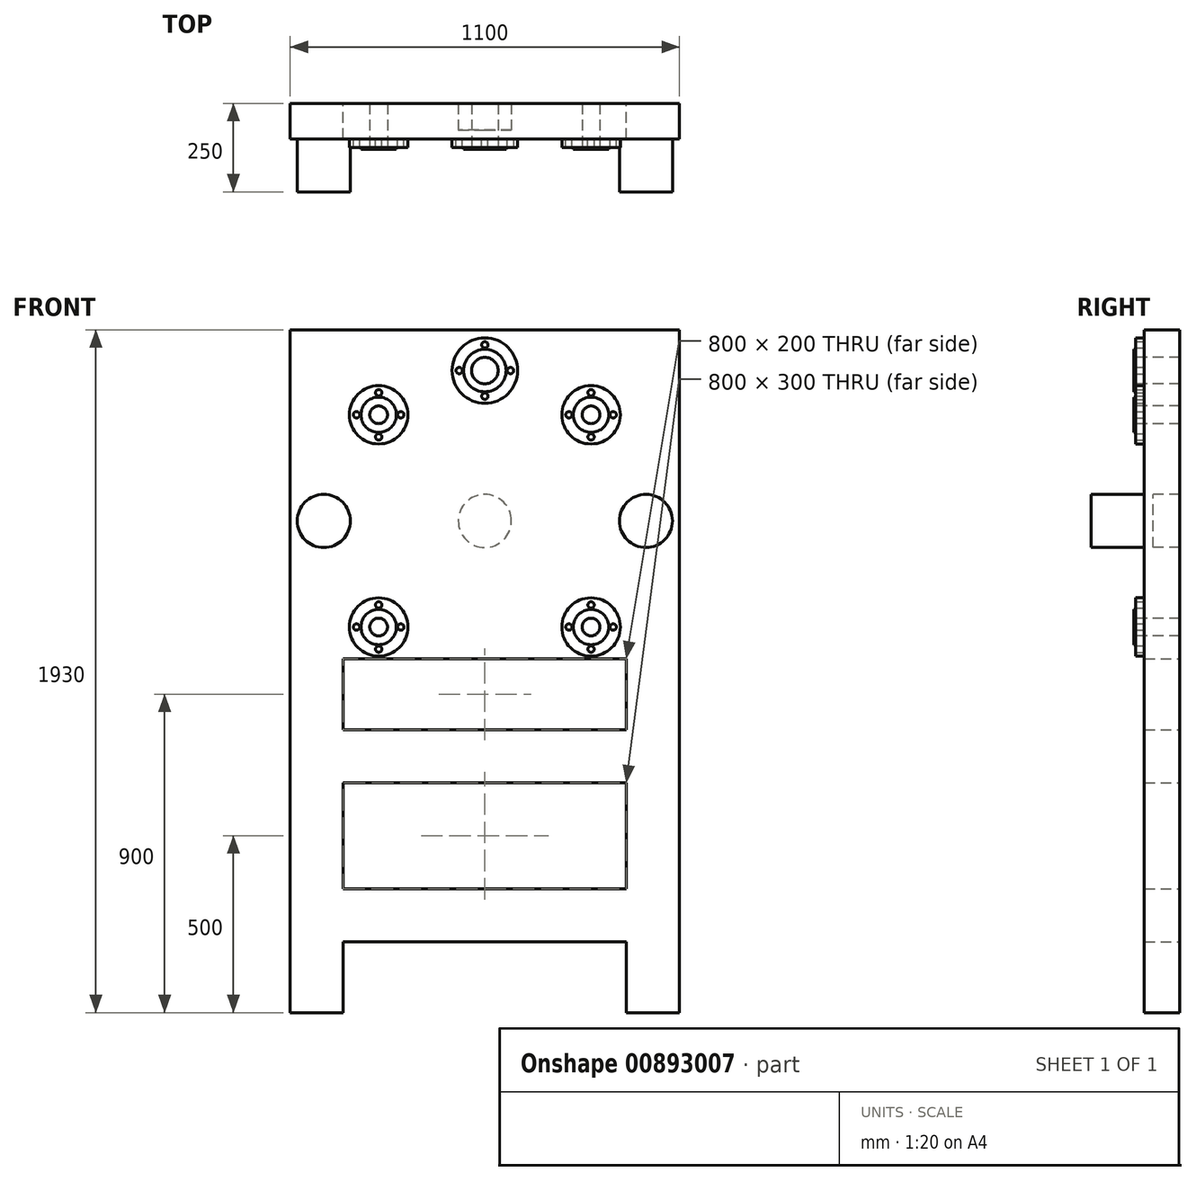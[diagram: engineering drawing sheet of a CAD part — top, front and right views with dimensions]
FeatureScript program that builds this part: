
annotation { "Feature Type Name" : "Feature", "Feature Type Description" : "" }
export const myFeature = defineFeature(function(context is Context, id is Id, definition is map)
    precondition{}
    {
        {
            var Q0;
            Q0=qCreatedBy(makeId("Front.planeOp"),FACE);
            var sketch = newSketch(context, id + "F0", { "sketchPlane" : qUnion([Q0])});
            skLineSegment(sketch, "E0.bottom", {"start": v(550, -965) * mm, "end": v(400, -965) * mm});
            skLineSegment(sketch, "E0.top", {"start": v(550, 965) * mm, "end": v(-550, 965) * mm});
            skLineSegment(sketch, "E0.left", {"start": v(550, -965) * mm, "end": v(550, 965) * mm});
            skLineSegment(sketch, "E0.right", {"start": v(-550, -965) * mm, "end": v(-550, 965) * mm});
            skPoint(sketch, "E0.middle", {"position": v(0, 0) * mm});
            skLineSegment(sketch, "E1.top", {"start": v(-400, -765) * mm, "end": v(400, -765) * mm});
            skLineSegment(sketch, "E1.left", {"start": v(-400, -965) * mm, "end": v(-400, -765) * mm});
            skLineSegment(sketch, "E1.right", {"start": v(400, -965) * mm, "end": v(400, -765) * mm});
            skLineSegment(sketch, "E2.bottom", {"start": v(-400, -615) * mm, "end": v(400, -615) * mm});
            skLineSegment(sketch, "E2.top", {"start": v(-400, -315) * mm, "end": v(400, -315) * mm});
            skLineSegment(sketch, "E2.left", {"start": v(-400, -615) * mm, "end": v(-400, -315) * mm});
            skLineSegment(sketch, "E2.right", {"start": v(400, -615) * mm, "end": v(400, -315) * mm});
            skLineSegment(sketch, "E3.trimOffspring", {"start": v(-400, -965) * mm, "end": v(-550, -965) * mm});
            skLineSegment(sketch, "E4.bottom", {"start": v(-400, -165) * mm, "end": v(400, -165) * mm});
            skLineSegment(sketch, "E4.top", {"start": v(-400, 35) * mm, "end": v(400, 35) * mm});
            skLineSegment(sketch, "E4.left", {"start": v(-400, -165) * mm, "end": v(-400, 35) * mm});
            skLineSegment(sketch, "E4.right", {"start": v(400, -165) * mm, "end": v(400, 35) * mm});
            skPoint(sketch, "E5.middle", {"position": v(0, 425) * mm});
            skSolve(sketch);
        }
        {
            var Q0;
            Q0=makeQuery(id+"F0.imprint","IMPRINT",FACE,{"disambiguationData":[TD([[makeQuery(id+"F0.imprint","IMPRINT",EDGE,{"derivedFrom":sQuery(id+"F0.wireOp",EDGE,"E0.bottom")}),-1.0]])]});
            extrude(context, id + "F1", {"entities" : qUnion([Q0]), "depth" : 100 * mm, "offsetDistance" : 25 * mm});
        }
        {
            var Q0;
            Q0=makeQuery(id+"F1.opExtrude","CAP_FACE",FACE,{"disambiguationData":[OSD([sQuery(id+"F0.wireOp",EDGE,"E0.bottom"),sQuery(id+"F0.wireOp",EDGE,"E0.top"),sQuery(id+"F0.wireOp",EDGE,"E0.left"),sQuery(id+"F0.wireOp",EDGE,"E0.right"),sQuery(id+"F0.wireOp",EDGE,"E1.top"),sQuery(id+"F0.wireOp",EDGE,"E1.left"),sQuery(id+"F0.wireOp",EDGE,"E1.right"),sQuery(id+"F0.wireOp",EDGE,"E2.bottom"),sQuery(id+"F0.wireOp",EDGE,"E2.top"),sQuery(id+"F0.wireOp",EDGE,"E2.left"),sQuery(id+"F0.wireOp",EDGE,"E2.right"),sQuery(id+"F0.wireOp",EDGE,"E3.trimOffspring"),sQuery(id+"F0.wireOp",EDGE,"nSGubIzk-R7de-6MO4-penA-cvBglKJnvsGC"),sQuery(id+"F0.wireOp",EDGE,"E4.bottom"),sQuery(id+"F0.wireOp",EDGE,"E4.top"),sQuery(id+"F0.wireOp",EDGE,"E4.left"),sQuery(id+"F0.wireOp",EDGE,"E4.right")])],"isStart":false});
            var sketch = newSketch(context, id + "F2", { "sketchPlane" : qUnion([Q0])});
            skCircle(sketch, "E6", {"center": v(-300, 125) * mm, "radius": 25 * mm});
            skCircle(sketch, "E7.0", {"center": v(0, 425) * mm, "radius": 75 * mm});
            skCircle(sketch, "E8.0.1.0", {"center": v(-300, 725) * mm, "radius": 25 * mm});
            skCircle(sketch, "E8.1.0.0", {"center": v(300, 125) * mm, "radius": 25 * mm});
            skCircle(sketch, "E8.1.1.0", {"center": v(300, 725) * mm, "radius": 25 * mm});
            skLineSegment(sketch, "E8.direction1", {"start": v(-300, 125) * mm, "end": v(300, 125) * mm, "construction": true});
            skLineSegment(sketch, "E8.direction2", {"start": v(-300, 125) * mm, "end": v(-300, 725) * mm, "construction": true});
            skSolve(sketch);
        }
        {
            var Q0;
            Q0=qSketchRegion(id+"F2",true);
            extrude(context, id + "F3", {"entities" : qUnion([Q0]), "operationType" : NewBodyOperationType.REMOVE, "oppositeDirection" : true, "depth" : 100 * mm, "offsetDistance" : 25 * mm});
        }
        {
            var Q0;
            Q0=makeQuery(id+"F1.opExtrude","CAP_FACE",FACE,{"disambiguationData":[OSD([sQuery(id+"F0.wireOp",EDGE,"E0.bottom"),sQuery(id+"F0.wireOp",EDGE,"E0.top"),sQuery(id+"F0.wireOp",EDGE,"E0.left"),sQuery(id+"F0.wireOp",EDGE,"E0.right"),sQuery(id+"F0.wireOp",EDGE,"E1.top"),sQuery(id+"F0.wireOp",EDGE,"E1.left"),sQuery(id+"F0.wireOp",EDGE,"E1.right"),sQuery(id+"F0.wireOp",EDGE,"E2.bottom"),sQuery(id+"F0.wireOp",EDGE,"E2.top"),sQuery(id+"F0.wireOp",EDGE,"E2.left"),sQuery(id+"F0.wireOp",EDGE,"E2.right"),sQuery(id+"F0.wireOp",EDGE,"E3.trimOffspring"),sQuery(id+"F0.wireOp",EDGE,"nSGubIzk-R7de-6MO4-penA-cvBglKJnvsGC"),sQuery(id+"F0.wireOp",EDGE,"E4.bottom"),sQuery(id+"F0.wireOp",EDGE,"E4.top"),sQuery(id+"F0.wireOp",EDGE,"E4.left"),sQuery(id+"F0.wireOp",EDGE,"E4.right")])],"isStart":false});
            var sketch = newSketch(context, id + "F4", { "sketchPlane" : qUnion([Q0])});
            skCircle(sketch, "E9", {"center": v(-455, 425) * mm, "radius": 75 * mm});
            skCircle(sketch, "E10.MirrorC", {"center": v(455, 425) * mm, "radius": 75 * mm});
            skSolve(sketch);
        }
        {
            var Q0;
            Q0=qSketchRegion(id+"F4",true);
            extrude(context, id + "F5", {"entities" : qUnion([Q0]), "operationType" : NewBodyOperationType.ADD, "depth" : 150 * mm, "offsetDistance" : 25 * mm});
        }
        {
            var Q0;
            Q0=makeQuery(id+"F1.opExtrude","CAP_FACE",FACE,{"disambiguationData":[OSD([sQuery(id+"F0.wireOp",EDGE,"E0.bottom"),sQuery(id+"F0.wireOp",EDGE,"E0.top"),sQuery(id+"F0.wireOp",EDGE,"E0.left"),sQuery(id+"F0.wireOp",EDGE,"E0.right"),sQuery(id+"F0.wireOp",EDGE,"E1.top"),sQuery(id+"F0.wireOp",EDGE,"E1.left"),sQuery(id+"F0.wireOp",EDGE,"E1.right"),sQuery(id+"F0.wireOp",EDGE,"E2.bottom"),sQuery(id+"F0.wireOp",EDGE,"E2.top"),sQuery(id+"F0.wireOp",EDGE,"E2.left"),sQuery(id+"F0.wireOp",EDGE,"E2.right"),sQuery(id+"F0.wireOp",EDGE,"E3.trimOffspring"),sQuery(id+"F0.wireOp",EDGE,"nSGubIzk-R7de-6MO4-penA-cvBglKJnvsGC"),sQuery(id+"F0.wireOp",EDGE,"E4.bottom"),sQuery(id+"F0.wireOp",EDGE,"E4.top"),sQuery(id+"F0.wireOp",EDGE,"E4.left"),sQuery(id+"F0.wireOp",EDGE,"E4.right")])],"isStart":false});
            var sketch = newSketch(context, id + "F6", { "sketchPlane" : qUnion([Q0])});
            skCircle(sketch, "E11", {"center": v(-300, 725) * mm, "radius": 82.5 * mm});
            skCircle(sketch, "E12", {"center": v(-300, 787.5) * mm, "radius": 9 * mm});
            skCircle(sketch, "E13.0", {"center": v(-300, 725) * mm, "radius": 25 * mm});
            skCircle(sketch, "E14.1.0", {"center": v(-362.5, 725) * mm, "radius": 9 * mm});
            skCircle(sketch, "E14.2.0", {"center": v(-300, 662.5) * mm, "radius": 9 * mm});
            skCircle(sketch, "E14.3.0", {"center": v(-237.5, 725) * mm, "radius": 9 * mm});
            skPoint(sketch, "E15.0.1.0", {"position": v(-300, 125) * mm});
            skCircle(sketch, "E15.0.1.1", {"center": v(-300, 125) * mm, "radius": 82.5 * mm});
            skCircle(sketch, "E15.0.1.2", {"center": v(-300, 125) * mm, "radius": 25 * mm});
            skCircle(sketch, "E15.0.1.3", {"center": v(-237.5, 125) * mm, "radius": 9 * mm});
            skCircle(sketch, "E15.0.1.4", {"center": v(-362.5, 125) * mm, "radius": 9 * mm});
            skCircle(sketch, "E15.0.1.5", {"center": v(-300, 187.5) * mm, "radius": 9 * mm});
            skCircle(sketch, "E15.0.1.6", {"center": v(-300, 62.5) * mm, "radius": 9 * mm});
            skPoint(sketch, "E15.1.0.0", {"position": v(300, 725) * mm});
            skCircle(sketch, "E15.1.0.1", {"center": v(300, 725) * mm, "radius": 82.5 * mm});
            skCircle(sketch, "E15.1.0.2", {"center": v(300, 725) * mm, "radius": 25 * mm});
            skCircle(sketch, "E15.1.0.3", {"center": v(362.5, 725) * mm, "radius": 9 * mm});
            skCircle(sketch, "E15.1.0.4", {"center": v(237.5, 725) * mm, "radius": 9 * mm});
            skCircle(sketch, "E15.1.0.5", {"center": v(300, 787.5) * mm, "radius": 9 * mm});
            skCircle(sketch, "E15.1.0.6", {"center": v(300, 662.5) * mm, "radius": 9 * mm});
            skPoint(sketch, "E15.1.1.0", {"position": v(300, 125) * mm});
            skCircle(sketch, "E15.1.1.1", {"center": v(300, 125) * mm, "radius": 82.5 * mm});
            skCircle(sketch, "E15.1.1.2", {"center": v(300, 125) * mm, "radius": 25 * mm});
            skCircle(sketch, "E15.1.1.3", {"center": v(362.5, 125) * mm, "radius": 9 * mm});
            skCircle(sketch, "E15.1.1.4", {"center": v(237.5, 125) * mm, "radius": 9 * mm});
            skCircle(sketch, "E15.1.1.5", {"center": v(300, 187.5) * mm, "radius": 9 * mm});
            skCircle(sketch, "E15.1.1.6", {"center": v(300, 62.5) * mm, "radius": 9 * mm});
            skLineSegment(sketch, "E15.direction1", {"start": v(-300, 662.5) * mm, "end": v(300, 662.5) * mm, "construction": true});
            skLineSegment(sketch, "E15.direction2", {"start": v(-300, 662.5) * mm, "end": v(-300, 62.5) * mm, "construction": true});
            skSolve(sketch);
        }
        {
            var Q0;
            Q0=qSketchRegion(id+"F6",true);
            extrude(context, id + "F7", {"entities" : qUnion([Q0]), "operationType" : NewBodyOperationType.ADD, "depth" : 25 * mm, "offsetDistance" : 25 * mm});
        }
        {
            var Q0;
            Q0=makeQuery(id+"F7.opExtrude","CAP_FACE",FACE,{"disambiguationData":[OSD([sQuery(id+"F6.wireOp",EDGE,"E11"),sQuery(id+"F6.wireOp",EDGE,"E12"),sQuery(id+"F6.wireOp",EDGE,"E13.0"),sQuery(id+"F6.wireOp",EDGE,"E14.1.0"),sQuery(id+"F6.wireOp",EDGE,"E14.2.0"),sQuery(id+"F6.wireOp",EDGE,"E14.3.0")])],"isStart":false});
            var sketch = newSketch(context, id + "F8", { "sketchPlane" : qUnion([Q0])});
            skCircle(sketch, "E16", {"center": v(-300, 725) * mm, "radius": 50 * mm});
            skCircle(sketch, "E17.0.1.0", {"center": v(-300, 125) * mm, "radius": 50 * mm});
            skCircle(sketch, "E17.1.0.0", {"center": v(300, 725) * mm, "radius": 50 * mm});
            skCircle(sketch, "E17.1.1.0", {"center": v(300, 125) * mm, "radius": 50 * mm});
            skLineSegment(sketch, "E17.direction1", {"start": v(-300, 725) * mm, "end": v(300, 725) * mm, "construction": true});
            skLineSegment(sketch, "E17.direction2", {"start": v(-300, 725) * mm, "end": v(-300, 125) * mm, "construction": true});
            skCircle(sketch, "E18", {"center": v(300, 725) * mm, "radius": 25 * mm});
            skCircle(sketch, "E19", {"center": v(300, 125) * mm, "radius": 25 * mm});
            skCircle(sketch, "E20", {"center": v(-300, 125) * mm, "radius": 25 * mm});
            skCircle(sketch, "E21", {"center": v(-300, 725) * mm, "radius": 25 * mm});
            skSolve(sketch);
        }
        {
            var Q0;
            Q0=qSketchRegion(id+"F8",true);
            extrude(context, id + "F9", {"entities" : qUnion([Q0]), "operationType" : NewBodyOperationType.ADD, "depth" : 5 * mm, "offsetDistance" : 25 * mm});
        }
        {
            var Q0;
            {var subQ0=sQuery(id+"F0.wireOp",EDGE,"E4.right");var subQ1=sQuery(id+"F0.wireOp",EDGE,"E4.left");var subQ2=sQuery(id+"F0.wireOp",EDGE,"E4.top");var subQ3=sQuery(id+"F0.wireOp",EDGE,"E1.left");var subQ4=sQuery(id+"F0.wireOp",EDGE,"E4.bottom");var subQ5=sQuery(id+"F0.wireOp",EDGE,"E3.trimOffspring");var subQ6=sQuery(id+"F0.wireOp",EDGE,"E2.right");var subQ7=sQuery(id+"F0.wireOp",EDGE,"E0.left");var subQ8=sQuery(id+"F0.wireOp",EDGE,"E0.top");var subQ9=sQuery(id+"F0.wireOp",EDGE,"E0.right");var subQ10=sQuery(id+"F0.wireOp",EDGE,"E2.bottom");var subQ11=sQuery(id+"F0.wireOp",EDGE,"E0.bottom");var subQ12=sQuery(id+"F0.wireOp",EDGE,"E2.left");var subQ13=sQuery(id+"F0.wireOp",EDGE,"E1.top");var subQ14=sQuery(id+"F0.wireOp",EDGE,"E1.right");var subQ15=sQuery(id+"F0.wireOp",EDGE,"E2.top");Q0=makeQuery(id+"F7.boolean.opBoolean","SPLIT",FACE,{"disambiguationData":[TD([makeQuery(id+"F1.opExtrude","SWEPT_FACE",FACE,{"disambiguationData":[OSD([subQ11])]})])],"derivedFrom":makeQuery(id+"F1.opExtrude","CAP_FACE",FACE,{"disambiguationData":[OSD([subQ11,subQ8,subQ7,subQ9,subQ13,subQ3,subQ14,subQ10,subQ15,subQ12,subQ6,subQ5,subQ4,subQ2,subQ1,subQ0])],"isStart":false})});}
            var sketch = newSketch(context, id + "F10", { "sketchPlane" : qUnion([Q0])});
            skCircle(sketch, "E22.0", {"center": v(0, 425) * mm, "radius": 75 * mm});
            skSolve(sketch);
        }
        {
            var Q0;
            Q0=qSketchRegion(id+"F10",true);
            extrude(context, id + "F11", {"entities" : qUnion([Q0]), "operationType" : NewBodyOperationType.ADD, "oppositeDirection" : true, "depth" : 25 * mm, "offsetDistance" : 25 * mm});
        }
        {
            var Q0;
            {var subQ0=sQuery(id+"F0.wireOp",EDGE,"E4.right");var subQ1=sQuery(id+"F0.wireOp",EDGE,"E4.left");var subQ2=sQuery(id+"F0.wireOp",EDGE,"E4.top");var subQ3=sQuery(id+"F0.wireOp",EDGE,"E1.left");var subQ4=sQuery(id+"F0.wireOp",EDGE,"E4.bottom");var subQ5=sQuery(id+"F0.wireOp",EDGE,"E3.trimOffspring");var subQ6=sQuery(id+"F0.wireOp",EDGE,"E2.right");var subQ7=sQuery(id+"F0.wireOp",EDGE,"E0.left");var subQ8=sQuery(id+"F0.wireOp",EDGE,"E0.top");var subQ9=sQuery(id+"F0.wireOp",EDGE,"E0.right");var subQ10=sQuery(id+"F0.wireOp",EDGE,"E2.bottom");var subQ11=sQuery(id+"F0.wireOp",EDGE,"E0.bottom");var subQ12=sQuery(id+"F0.wireOp",EDGE,"E2.left");var subQ13=sQuery(id+"F0.wireOp",EDGE,"E1.top");var subQ14=sQuery(id+"F0.wireOp",EDGE,"E1.right");var subQ15=sQuery(id+"F0.wireOp",EDGE,"E2.top");Q0=makeQuery(id+"F11.boolean.opBoolean","MERGE",FACE,{"derivedFrom":[makeQuery(id+"F7.boolean.opBoolean","SPLIT",FACE,{"disambiguationData":[TD([makeQuery(id+"F1.opExtrude","SWEPT_FACE",FACE,{"disambiguationData":[OSD([subQ11])]})])],"derivedFrom":makeQuery(id+"F1.opExtrude","CAP_FACE",FACE,{"disambiguationData":[OSD([subQ11,subQ8,subQ7,subQ9,subQ13,subQ3,subQ14,subQ10,subQ15,subQ12,subQ6,subQ5,subQ4,subQ2,subQ1,subQ0])],"isStart":false})}),makeQuery(id+"F11.opExtrude","CAP_FACE",FACE,{"disambiguationData":[OSD([sQuery(id+"F10.wireOp",EDGE,"E22.0")])],"isStart":true})]});}
            var sketch = newSketch(context, id + "F12", { "sketchPlane" : qUnion([Q0])});
            skCircle(sketch, "E23", {"center": v(0, 850) * mm, "radius": 37.5 * mm});
            skPoint(sketch, "E23.centerSnap0", {"position": v(0, 965) * mm});
            skCircle(sketch, "E24.0", {"center": v(300, 725) * mm, "radius": 25 * mm});
            skSolve(sketch);
        }
        {
            var Q0;
            Q0=makeQuery(id+"F12.imprint","IMPRINT",FACE,{"disambiguationData":[TD([[makeQuery(id+"F12.imprint","IMPRINT",EDGE,{"derivedFrom":sQuery(id+"F12.wireOp",EDGE,"E23")}),1.0]])]});
            extrude(context, id + "F13", {"entities" : qUnion([Q0]), "operationType" : NewBodyOperationType.REMOVE, "oppositeDirection" : true, "depth" : 100 * mm, "offsetDistance" : 25 * mm});
        }
        {
            var Q0;
            {var subQ0=sQuery(id+"F0.wireOp",EDGE,"E4.right");var subQ1=sQuery(id+"F0.wireOp",EDGE,"E4.left");var subQ2=sQuery(id+"F0.wireOp",EDGE,"E4.top");var subQ3=sQuery(id+"F0.wireOp",EDGE,"E1.left");var subQ4=sQuery(id+"F0.wireOp",EDGE,"E4.bottom");var subQ5=sQuery(id+"F0.wireOp",EDGE,"E3.trimOffspring");var subQ6=sQuery(id+"F0.wireOp",EDGE,"E2.right");var subQ7=sQuery(id+"F0.wireOp",EDGE,"E0.left");var subQ8=sQuery(id+"F0.wireOp",EDGE,"E0.top");var subQ9=sQuery(id+"F0.wireOp",EDGE,"E0.right");var subQ10=sQuery(id+"F0.wireOp",EDGE,"E2.bottom");var subQ11=sQuery(id+"F0.wireOp",EDGE,"E0.bottom");var subQ12=sQuery(id+"F0.wireOp",EDGE,"E2.left");var subQ13=sQuery(id+"F0.wireOp",EDGE,"E1.top");var subQ14=sQuery(id+"F0.wireOp",EDGE,"E1.right");var subQ15=sQuery(id+"F0.wireOp",EDGE,"E2.top");Q0=makeQuery(id+"F11.boolean.opBoolean","MERGE",FACE,{"derivedFrom":[makeQuery(id+"F7.boolean.opBoolean","SPLIT",FACE,{"disambiguationData":[TD([makeQuery(id+"F1.opExtrude","SWEPT_FACE",FACE,{"disambiguationData":[OSD([subQ11])]})])],"derivedFrom":makeQuery(id+"F1.opExtrude","CAP_FACE",FACE,{"disambiguationData":[OSD([subQ11,subQ8,subQ7,subQ9,subQ13,subQ3,subQ14,subQ10,subQ15,subQ12,subQ6,subQ5,subQ4,subQ2,subQ1,subQ0])],"isStart":false})}),makeQuery(id+"F11.opExtrude","CAP_FACE",FACE,{"disambiguationData":[OSD([sQuery(id+"F10.wireOp",EDGE,"E22.0")])],"isStart":true})]});}
            var sketch = newSketch(context, id + "F14", { "sketchPlane" : qUnion([Q0])});
            skCircle(sketch, "E25", {"center": v(0, 850) * mm, "radius": 92.5 * mm});
            skCircle(sketch, "E26", {"center": v(0, 922.5) * mm, "radius": 9 * mm});
            skCircle(sketch, "E27.1.0", {"center": v(-72.5, 850) * mm, "radius": 9 * mm});
            skCircle(sketch, "E27.2.0", {"center": v(0, 777.5) * mm, "radius": 9 * mm});
            skCircle(sketch, "E27.3.0", {"center": v(72.5, 850) * mm, "radius": 9 * mm});
            skSolve(sketch);
        }
        {
            var Q0;
            Q0=makeQuery(id+"F14.imprint","IMPRINT",FACE,{"disambiguationData":[TD([[makeQuery(id+"F14.imprint","IMPRINT",EDGE,{"derivedFrom":sQuery(id+"F14.wireOp",EDGE,"E25")}),1.0]])]});
            extrude(context, id + "F15", {"entities" : qUnion([Q0]), "operationType" : NewBodyOperationType.ADD, "depth" : 25 * mm, "offsetDistance" : 25 * mm});
        }
        {
            var Q0;
            Q0=makeQuery(id+"F15.opExtrude","CAP_FACE",FACE,{"disambiguationData":[OSD([sQuery(id+"F12.wireOp",EDGE,"E23"),sQuery(id+"F14.wireOp",EDGE,"E25"),sQuery(id+"F14.wireOp",EDGE,"E26"),sQuery(id+"F14.wireOp",EDGE,"E27.1.0"),sQuery(id+"F14.wireOp",EDGE,"E27.2.0"),sQuery(id+"F14.wireOp",EDGE,"E27.3.0")])],"isStart":false});
            var sketch = newSketch(context, id + "F16", { "sketchPlane" : qUnion([Q0])});
            skCircle(sketch, "E28", {"center": v(0, 850) * mm, "radius": 60 * mm});
            skSolve(sketch);
        }
        {
            var Q0;
            Q0=makeQuery(id+"F16.imprint","IMPRINT",FACE,{"disambiguationData":[TD([[makeQuery(id+"F16.imprint","IMPRINT",EDGE,{"derivedFrom":sQuery(id+"F16.wireOp",EDGE,"E28")}),1.0]])]});
            extrude(context, id + "F17", {"entities" : qUnion([Q0]), "operationType" : NewBodyOperationType.ADD, "depth" : 5 * mm, "offsetDistance" : 25 * mm});
        }
    });
